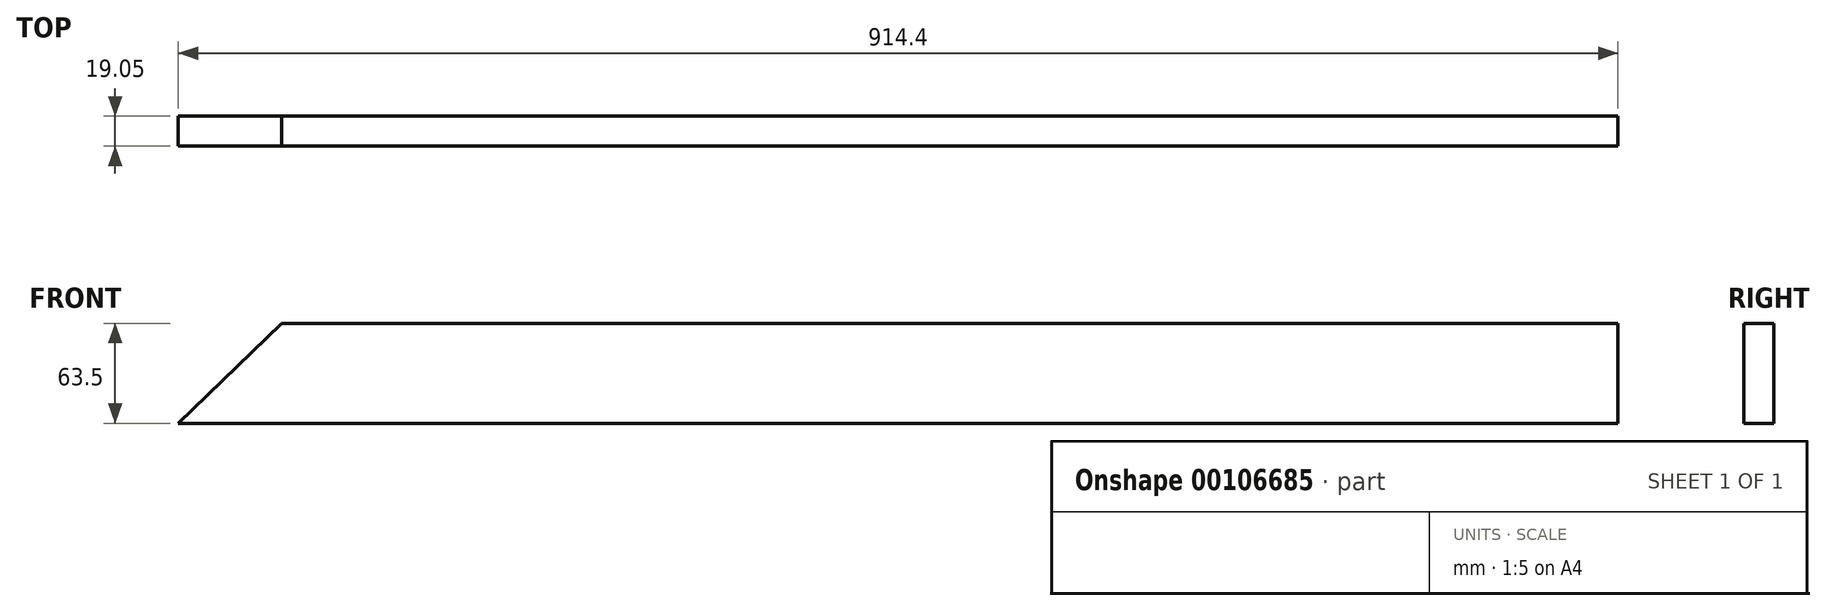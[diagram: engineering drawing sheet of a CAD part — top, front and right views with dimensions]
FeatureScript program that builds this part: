
annotation { "Feature Type Name" : "Feature", "Feature Type Description" : "" }
export const myFeature = defineFeature(function(context is Context, id is Id, definition is map)
    precondition{}
    {
        {
            var Q0;
            Q0=qCreatedBy(makeId("Front.planeOp"),FACE);
            var sketch = newSketch(context, id + "F0", { "sketchPlane" : qUnion([Q0])});
            skLineSegment(sketch, "E0.bottom", {"start": v(0, 0) * mm, "end": v(914.4, 0) * mm});
            skLineSegment(sketch, "E0.top", {"start": v(65.55, 63.5) * mm, "end": v(914.4, 63.5) * mm});
            skLineSegment(sketch, "E0.right", {"start": v(914.4, 0) * mm, "end": v(914.4, 63.5) * mm});
            skLineSegment(sketch, "E1", {"start": v(0, 0) * mm, "end": v(65.55, 63.5) * mm});
            skSolve(sketch);
        }
        {
            var Q0;
            Q0=makeQuery(id+"F0.imprint","IMPRINT",FACE,{"disambiguationData":[TD([[makeQuery(id+"F0.imprint","IMPRINT",EDGE,{"derivedFrom":sQuery(id+"F0.wireOp",EDGE,"E0.bottom")}),1.0]])]});
            extrude(context, id + "F1", {"entities" : qUnion([Q0]), "depth" : 19.05 * mm});
        }
    });
